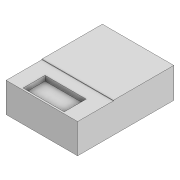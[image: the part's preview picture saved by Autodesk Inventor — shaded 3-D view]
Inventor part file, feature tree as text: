
AUTODESK INVENTOR PART (.ipt)
format: ipt  version: 2022 (Build 260153000, 153)  size: 122,880 bytes
history: native  units: mm
features: extrude x4, sketch x4, projected_geometry x3
ambient origin geometry x8: Origin, YZ Plane, XZ Plane, XY Plane, X Axis, Y Axis, Z Axis, Center Point
bodies: Volumenkörper1 (feature_tree)
feature tree (11):
  extrude  "Extrusion1"  Depth=17.5mm
  extrude  "Extrusion2"  Depth=7.5mm
  extrude  "Extrusion3"  Depth=1.0mm TaperAngle=0.0deg
  extrude  "Extrusion4"  Depth=0.1mm TaperAngle=0.0deg
  sketch  "Skizze1"  dims[d0=13.0mm d1=17.5mm]
  sketch  "Skizze2"  dims[d2=5.5mm d3=0.0mm d4=7.5mm]
  projected_geometry  "Projizierte Kontur1"
  sketch  "Skizze3"  dims[d5=4.0mm d6=1.0mm d7=0.0mm]
  projected_geometry  "Projizierte Kontur2"
  sketch  "Skizze4"  dims[d8=6.5mm d9=0.1mm d10=0.0mm d11=7.3mm d12=4.0mm d13=0.1mm d14=0.0mm]
  projected_geometry  "Projizierte Kontur3"
